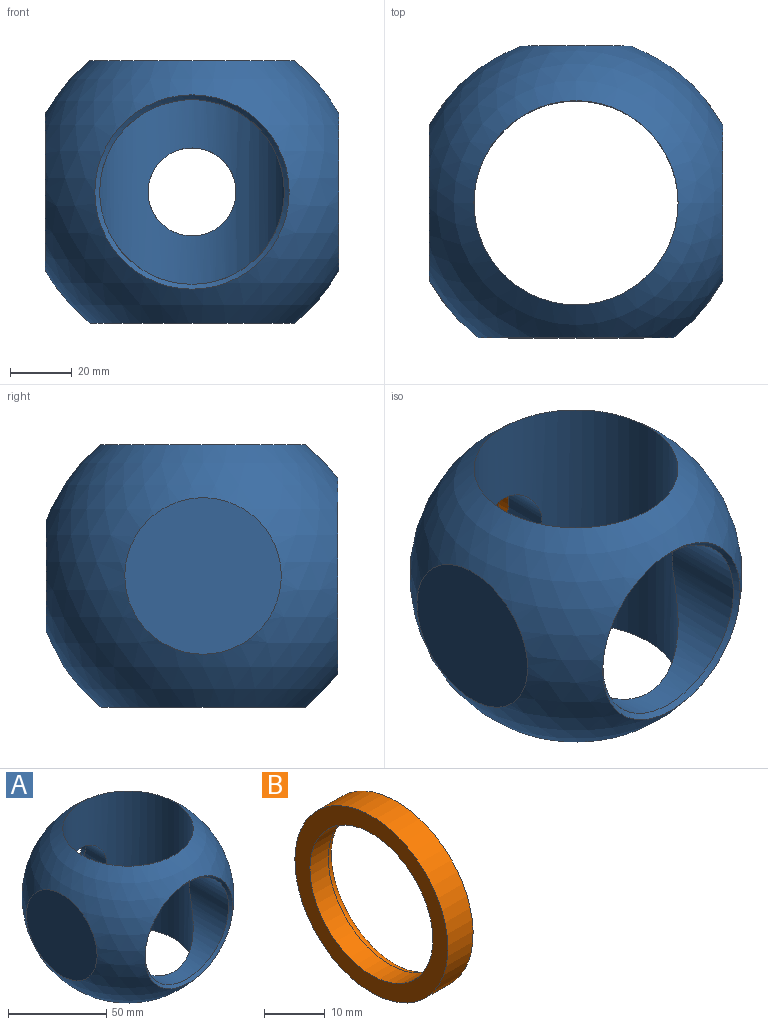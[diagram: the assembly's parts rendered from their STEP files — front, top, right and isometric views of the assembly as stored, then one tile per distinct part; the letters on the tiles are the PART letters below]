
ASSEMBLY  parts=2 mates=1
PART A: 9 faces, bbox 108x108x85.2 mm
  f0: sphere r=53.98mm, area 20111.7mm2, adj f1,f2,f3,f5,f6
  f1: plane 50.8x50.8mm, normal (1,0,0), area 2026.8mm2, adj f0
  f2: plane 50.8x50.8mm, normal (-1,0,0), area 2026.8mm2, adj f0
  f3: cylinder r=33.15mm len=85.2mm, axis (0,0,1), area 13792.2mm2, adj f0,f4,f8
  f4: cylinder r=29.97mm len=59.94mm, axis (0,-1,0), area 3331.7mm2, adj f3,f5
  f5: cone r=29.97mm half-angle=46.7deg, axis (0,-1,0), area 418.7mm2, adj f0,f4
  f6: cylinder r=17.78mm len=35.56mm, axis (0,1,0), area 656.6mm2, adj f0,f7
  f7: plane 35.56x35.56mm, normal (0,1,0), area 351.8mm2, adj f6,f8
  f8: cylinder r=14.29mm len=28.58mm, axis (0,1,0), area 1215.5mm2, adj f3,f7
PART B: 5 faces, bbox 5.9x35.6x35.6 mm
  f0: cylinder r=14.29mm len=28.58mm, axis (-1,0,0), area 384.2mm2, adj f3,f4
  f1: cylinder r=17.78mm len=35.56mm, axis (-1,0,0), area 655.5mm2, adj f2,f3
  f2: plane 35.56x35.56mm, normal (1,0,0), area 201.4mm2, adj f1,f4
  f3: plane 35.56x35.56mm, normal (-1,0,0), area 351.8mm2, adj f0,f1
  f4: torus R=15.88mm, axis (1,0,0), area 232.9mm2, adj f0,f2
PLACE A t=(0.03,0.21,0.17)mm
PLACE B rot(axis=(0,0,1),90deg) t=(0.03,45.3,0.17)mm
MATE fastened B.f1 <-> A.f6  axis (0,-1,0) through (0.03,48.23,0.17)mm
